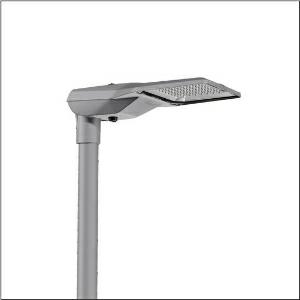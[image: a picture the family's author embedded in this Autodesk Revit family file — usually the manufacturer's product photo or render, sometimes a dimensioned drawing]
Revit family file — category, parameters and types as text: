
# Revit family: streetlight_sl_21_midi___st0_8a_5xe3c63t08lb_8787
name_source: partatom
category: Lighting Fixtures
units: mm (PartAtom-declared; Revit-internal decimal feet)

## family parameters
Cut with Voids When Loaded = No
Host = Face
Light Source = No
Part Type = Normal
Room Calculation Point = No
Round Connector Dimension = Use Diameter
Shared = No

## types (1)
- --- (1 x LED, 12860 lm, 99.6 W, 2700K)
    Apparent Load = 100 VA
    CIE Flux Codes = 38 75 97 100 100
    Color Rendering = 70
    Color Temperature = 2700K
    Default Elevation = 1800 mm
    Description = Streetlight SL 21 midi, mast luminaire, primary light control with lens, of PMMA, primary optical cover: cover, of toughened safety glass, transparent, light distribution: ST0.8a, light emission: direct distribution, primary light characteristic: asymmetric, installation type: side-entry, post-top, LED, High Power LED, rated luminous flux: 12.860lm, luminous efficacy: 129lm/W, light colour: 727, colour temperature: 2700K, control gear: D4i, control: overheat protection, constant luminous flux control, time-dependent luminous flux control, flexible luminous flux parameterisation, pre-setting: logarithmic dimming characteristic, mains connection: 230..240V, AC, 50/60Hz, start of lifetime: 100W, end of service life: 102W, reduction: 45W, luminaire housing, of diecast aluminium, powder-coated, Siteco® metallic grey (DB 702S), corrosivity category C5 mid according to DIN EN ISO 12944, please order mast flange separately, inclination adjustable: 0°, 5°, 10°, 15°, sealing non-destructively replaceable, multi-level sealing system, length: 644mm, width: 335mm, height: 110mm, mast flange for spigot size: 42mm (side-entry): 5XC10008XM4, 60/48mm (side-entry/post-top): 5XC10108XM2, 76/60mm (side-entry/post-top): 5XC10108XM1, mounting height: 4..8m, Smart Interface below and above, protection rating (complete): IP66, insulation class (complete): insulation class II (safety insulation), certification: CE, ENEC, ENEC+, VDE, impact resistance: IK10, permissible operating ambient temperature for outdoor applications: -40..+50°C, standard-compliant lighting for roads and squares, packaging unit: 1 piece

Light Distribution: ST0.8a
    Height = 111 mm
    Lamp = 1 x LED
    Lamp Light Flux = 12860 lm
    Lamp Power = 99.6 W
    Lamp count = 1
    Length = 644 mm
    Luminous efficacy = 129 lm/W
    Manufacturer = Siteco
    ModVariant = No
    Model = 5XE3C63T08LB
    Number of Poles = 1
    OnlyDefault = Yes
    Power Factor = 1
    Product Name = Streetlight SL 21 midi | ST0.8a
    Product group = mast luminaire | pylon top
    ProductGroupID = 6100
    Protection Class = Protection class II
    Protection Degree = IP 66
    RLX_Detail_Level = 1
    RLX_Emergency_Light_Flux = 0 lm
    RLX_Emergency_Type = 0
    RLX_Emergency_Type_DB = No
    RlxData = <blob elided: 26985 chars, md5=26a10f85>
    Socket = socket
    Standby Power = 0 W
    System Light Flux = 12860 lm
    System Power = 100 W
    Type Comments = factory setting: luminous flux: 100 % | dim-lin: 254 | 1020 mA
    Type Image = l_1004304.jpg
    URL = http://relux.com
    VarID = @adj_031173
    Voltage = 0 V
    Weight = 0.00 kg
    Width = 336 mm

## geometry (parser evidence)
native form markers: Blend x4, Sweep x9
no freeform markers — native parametric forms only
